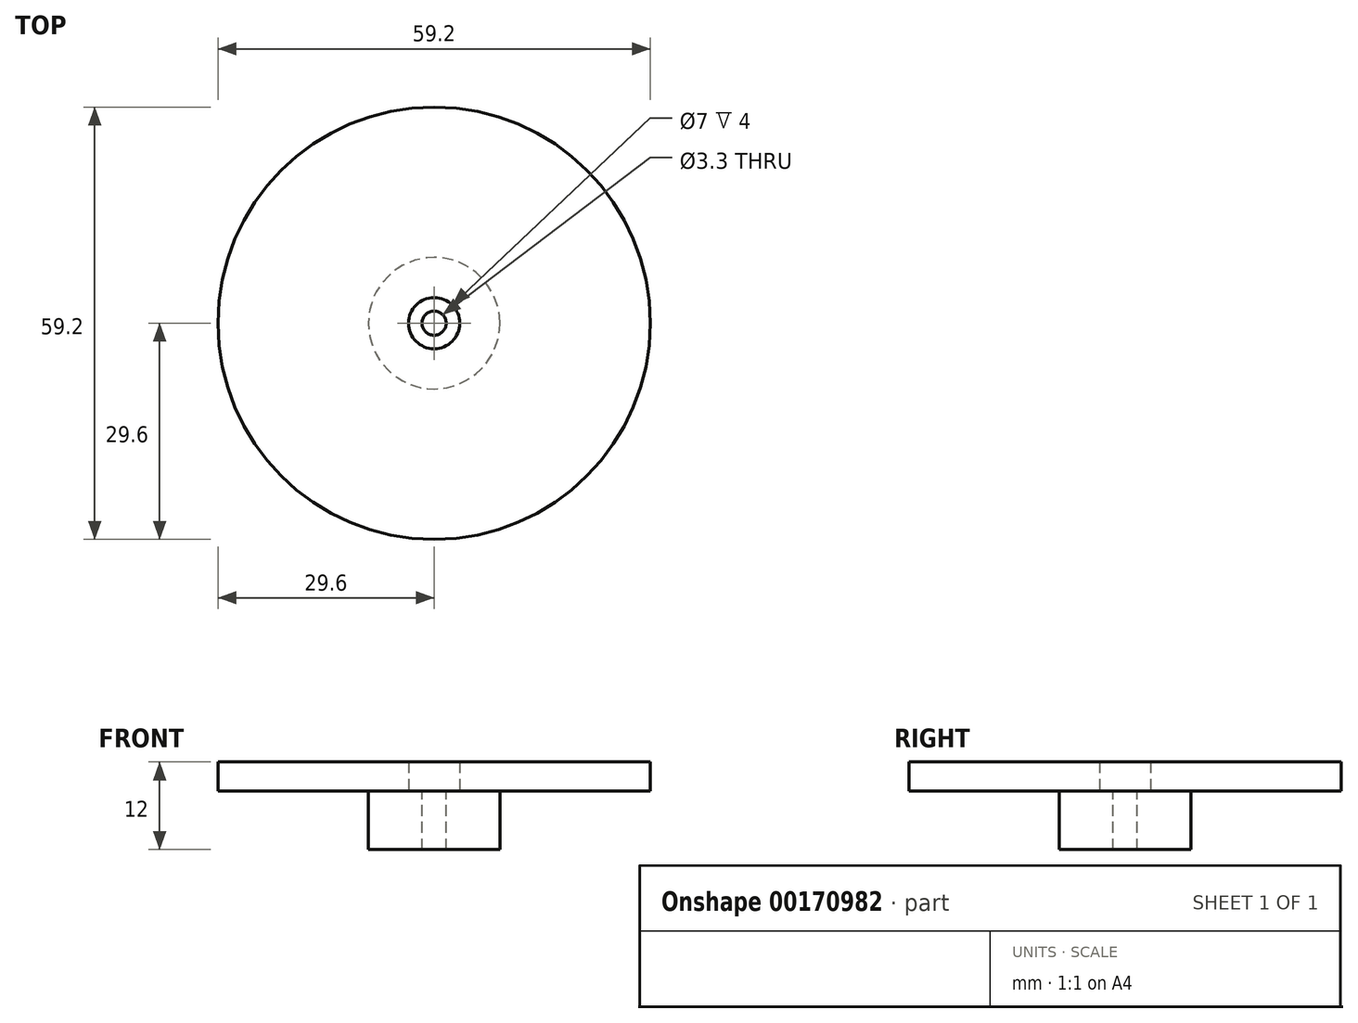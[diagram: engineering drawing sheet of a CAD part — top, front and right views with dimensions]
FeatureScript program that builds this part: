
annotation { "Feature Type Name" : "Feature", "Feature Type Description" : "" }
export const myFeature = defineFeature(function(context is Context, id is Id, definition is map)
    precondition{}
    {
        {
            var Q0;
            Q0=qCreatedBy(makeId("Top.planeOp"),FACE);
            var sketch = newSketch(context, id + "F0", { "sketchPlane" : qUnion([Q0])});
            skCircle(sketch, "E0", {"center": v(0, 0) * mm, "radius": 29.6 * mm});
            skCircle(sketch, "E1", {"center": v(0, 0) * mm, "radius": 9 * mm});
            skCircle(sketch, "E2", {"center": v(0, 0) * mm, "radius": 1.65 * mm});
            skCircle(sketch, "E3", {"center": v(0, 0) * mm, "radius": 3.5 * mm});
            skSolve(sketch);
        }
        {
            var Q0;
            Q0=makeQuery(id+"F0.imprint","IMPRINT",FACE,{"disambiguationData":[TD([[makeQuery(id+"F0.imprint","IMPRINT",EDGE,{"derivedFrom":sQuery(id+"F0.wireOp",EDGE,"E0")}),1.0]])]});
            var Q1;
            Q1=makeQuery(id+"F0.imprint","IMPRINT",FACE,{"disambiguationData":[TD([[makeQuery(id+"F0.imprint","IMPRINT",EDGE,{"derivedFrom":sQuery(id+"F0.wireOp",EDGE,"E1")}),1.0]])]});
            extrude(context, id + "F1", {"entities" : qUnion([Q0, Q1]), "depth" : 4 * mm});
        }
        {
            var Q0;
            Q0=makeQuery(id+"F0.imprint","IMPRINT",FACE,{"disambiguationData":[TD([[makeQuery(id+"F0.imprint","IMPRINT",EDGE,{"derivedFrom":sQuery(id+"F0.wireOp",EDGE,"E1")}),1.0]])]});
            var Q1;
            Q1=makeQuery(id+"F0.imprint","IMPRINT",FACE,{"disambiguationData":[TD([[makeQuery(id+"F0.imprint","IMPRINT",EDGE,{"derivedFrom":sQuery(id+"F0.wireOp",EDGE,"E2")}),-1.0]])]});
            extrude(context, id + "F2", {"entities" : qUnion([Q0, Q1]), "operationType" : NewBodyOperationType.ADD, "oppositeDirection" : true, "depth" : 8 * mm});
        }
    });
